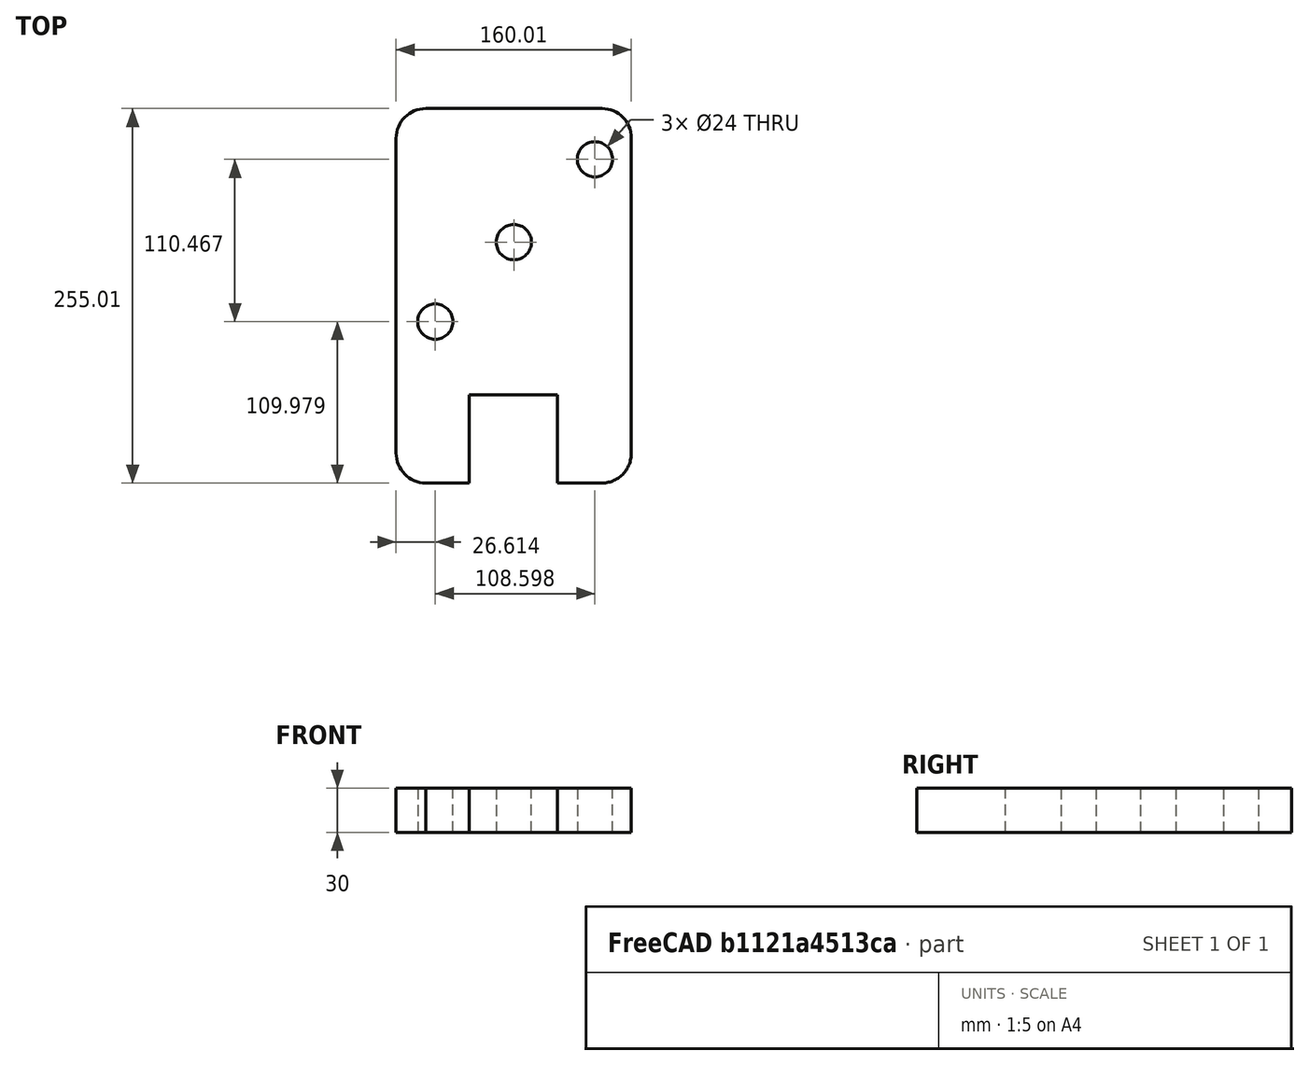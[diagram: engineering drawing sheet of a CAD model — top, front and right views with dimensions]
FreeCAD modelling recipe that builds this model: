
FCSTD DOCUMENT  (FreeCAD 0.18R16131 (Git))
Label: Momentum_Main(2)_Plate_1-3_160X255_12T_12mm(lm12uu)
License: All rights reserved
LicenseURL: http://en.wikipedia.org/wiki/All_rights_reserved
objects: PartDesign::Pad×2, Sketcher::SketchObject×1, PartDesign::Body×1
note: 6 computed .brp shape members not serialized (recipe doc carries the construction recipe); baked Part::Feature solids carry a one-line shape summary decoded from their .brp

FEATURE [Sketcher::SketchObject] Sketch
  MapMode = 5
  Support = -> [XY_Plane]
  sketch-geometry (15):
    g0: Circle CenterX=0.120778 CenterY=29.9192 CenterZ=0 NormalX=0 NormalY=0 NormalZ=1 AngleXU=0 Radius=12
    g1: Circle CenterX=-53.3259 CenterY=-24.1714 CenterZ=0 NormalX=0 NormalY=0 NormalZ=1 AngleXU=0 Radius=12
    g2: Circle CenterX=55.2719 CenterY=86.2952 CenterZ=0 NormalX=0 NormalY=0 NormalZ=1 AngleXU=0 Radius=12
    g3: LineSegment StartX=29.8086 StartY=-133.971 StartZ=0 EndX=29.8086 EndY=-73.9708 EndZ=0
    g4: LineSegment StartX=29.8086 StartY=-73.9708 StartZ=0 EndX=-30.1914 EndY=-73.9708 EndZ=0
    g5: LineSegment StartX=-30.1914 StartY=-73.9708 StartZ=0 EndX=-30.1914 EndY=-133.971 EndZ=0
    g6: LineSegment StartX=80.0689 StartY=-113.592 StartZ=0 EndX=80.0689 EndY=100.876 EndZ=0
    g7: LineSegment StartX=60.081 StartY=120.864 StartZ=0 EndX=-59.6856 EndY=120.864 EndZ=0
    g8: LineSegment StartX=-79.9439 StartY=100.605 StartZ=0 EndX=-79.9439 EndY=-113.553 EndZ=0
    g9: ArcOfCircle CenterX=60.081 CenterY=100.876 CenterZ=0 NormalX=0 NormalY=0 NormalZ=1 AngleXU=0 Radius=19.9878 StartAngle=0 EndAngle=1.5708
    g10: ArcOfCircle CenterX=-59.6856 CenterY=100.605 CenterZ=0 NormalX=0 NormalY=0 NormalZ=1 AngleXU=0 Radius=20.2583 StartAngle=1.5708 EndAngle=3.14159
    g11: ArcOfCircle CenterX=59.5166 CenterY=-113.592 CenterZ=0 NormalX=0 NormalY=0 NormalZ=1 AngleXU=0 Radius=20.5523 StartAngle=4.71233 EndAngle=6.28319
    g12: ArcOfCircle CenterX=-59.3423 CenterY=-113.553 CenterZ=0 NormalX=0 NormalY=0 NormalZ=1 AngleXU=0 Radius=20.6016 StartAngle=3.14159 EndAngle=4.68541
    g13: LineSegment StartX=-59.898 StartY=-134.147 StartZ=0 EndX=-30.1914 EndY=-133.971 EndZ=0
    g14: LineSegment StartX=29.8086 StartY=-133.971 StartZ=0 EndX=59.5153 EndY=-134.144 EndZ=0
  constraints (27):
    c: Radius(g0) = 12
    c: Radius(g1) = 12
    c: Radius(g2) = 12
    c: Coincident(g3,g4)
    c: Coincident(g4,g5)
    c: Horizontal(g4)
    c: Vertical(g3)
    c: Vertical(g5)
    c: DistanceX(g4,g4) = 60
    c: DistanceY(g3,g3) = 60
    c: Horizontal(g7)
    c: Vertical(g6)
    c: Vertical(g8)
    c: Tangent(g7,g9) = -1.5708
    c: Tangent(g6,g9) = -1.5708
    c: Tangent(g7,g10) = -1.5708
    c: Tangent(g8,g10) = -1.5708
    c: Tangent(g6,g11) = -1.5708
    c: Tangent(g8,g12) = -1.5708
    c: DistanceY(g5,g5) = 60
    c: Equal(g13,g14)
    c: Coincident(g5,g13)
    c: Coincident(g3,g14)
    c: Equal(g13,g14)
    c: Coincident(g11,g14)
    c: Coincident(g12,g13)
    c: Equal(g13,g14)
FEATURE [PartDesign::Pad] Pad
  Length = 30
  Length2 = 100
  Profile = -> Sketch
  Type = 0
FEATURE [PartDesign::Pad] Pad001
  BaseFeature = -> Pad
  Length = 30
  Length2 = 100
  Profile = -> Sketch
  Type = 0
FEATURE [PartDesign::Body] Body
  Group = -> [Sketch,Pad,Pad001]
  Origin = -> Origin
  Tip = -> Pad001
